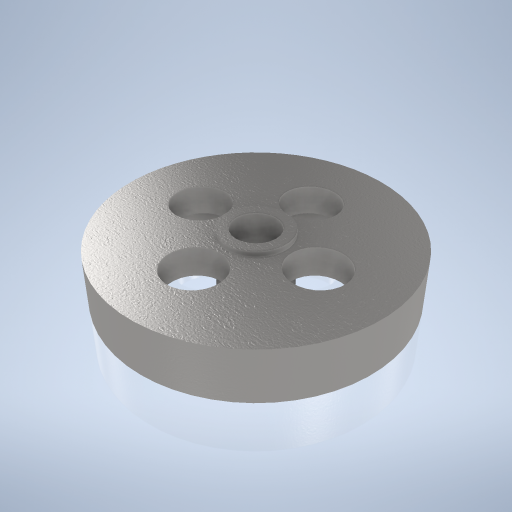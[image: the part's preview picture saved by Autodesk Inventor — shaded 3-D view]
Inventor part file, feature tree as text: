
AUTODESK INVENTOR PART (.ipt)
format: ipt  version: 2024.2 (Build 282272000, 272)  size: 345,600 bytes
history: native  units: mm
features: sketch x4, hole x2, revolve x1, extrude x1, pattern_circular x1
ambient origin geometry x8: Origin, YZ Plane, XZ Plane, XY Plane, X Axis, Y Axis, Z Axis, Center Point
bodies: Body1 (feature_tree)
feature tree (9):
  revolve  "Umdrehung1"
  extrude  "Extrusion3"  Depth=1.0mm
  hole  "Bohrung1"  [1 undecoded]
  hole  "Bohrung2"  [1 undecoded]
  pattern_circular  "Runde Anordnung1"  Count=4 Angle=360.0deg
  sketch  "Skizze4"  dims[d6=50.0mm d7=1.0mm]
  sketch  "Skizze5"  dims[d8=10.0mm d11=12.0mm]
  sketch  "Skizze6"  dims[d19=360.0deg d20=36.0mm]
  sketch  "Skizze7"  dims[d21=4.0mm d22=0.0mm d23=8.0mm d24=6.0mm d25=4.0mm d26=2.0mm d27=90.0deg d28=8.0mm d29=20.594885mm d32=10.0mm d33=6.0mm d34=4.0mm d35=2.0mm d36=90.0deg d37=8.0mm d38=20.594885mm d39=40.0mm d40=360.0deg d42=24.0mm]
note: 2 required parameter values undecoded (feature->parameter linkage not recoverable at this tier; creation-order binding heuristic only, values carry confidence <= 0.55)
